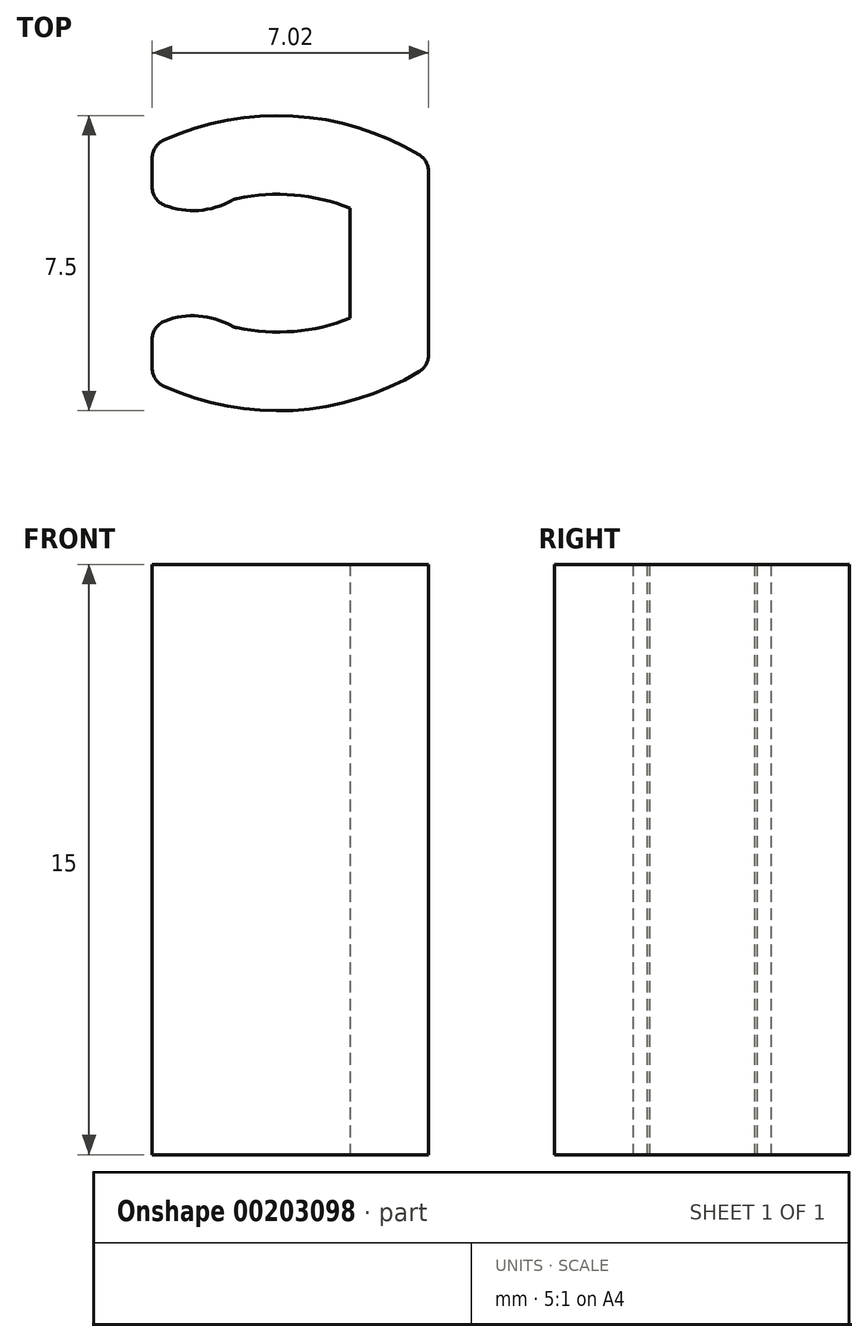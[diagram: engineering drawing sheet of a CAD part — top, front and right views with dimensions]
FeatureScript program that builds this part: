
annotation { "Feature Type Name" : "Feature", "Feature Type Description" : "" }
export const myFeature = defineFeature(function(context is Context, id is Id, definition is map)
    precondition{}
    {
        {
            var Q0;
            Q0=qCreatedBy(makeId("Top.planeOp"),FACE);
            var sketch = newSketch(context, id + "F0", { "sketchPlane" : qUnion([Q0])});
            skLineSegment(sketch, "E0", {"start": v(0, -23.14) * mm, "end": v(0, -17.14) * mm});
            skLineSegment(sketch, "E1", {"start": v(0, -17.14) * mm, "end": v(-4.2, -17.14) * mm});
            skLineSegment(sketch, "E2", {"start": v(-4.2, -17.14) * mm, "end": v(-3.62, -18.14) * mm});
            skLineSegment(sketch, "E3", {"start": v(0, -23.14) * mm, "end": v(-4.2, -23.14) * mm});
            skLineSegment(sketch, "E4", {"start": v(-4.2, -23.14) * mm, "end": v(-3.63, -22.15) * mm});
            skLineSegment(sketch, "E5.0", {"start": v(2, -15.14) * mm, "end": v(-4.2, -15.14) * mm});
            skLineSegment(sketch, "E5.1", {"start": v(2, -25.14) * mm, "end": v(2, -15.14) * mm});
            skLineSegment(sketch, "E5.2", {"start": v(2, -25.14) * mm, "end": v(-4.2, -25.14) * mm});
            skLineSegment(sketch, "E6", {"start": v(-3.63, -22.15) * mm, "end": v(-5.63, -22.15) * mm});
            skLineSegment(sketch, "E7", {"start": v(-5.63, -22.15) * mm, "end": v(-5.63, -24.15) * mm});
            skLineSegment(sketch, "E8", {"start": v(-5.63, -24.15) * mm, "end": v(-4.2, -25.14) * mm});
            skLineSegment(sketch, "E9", {"start": v(-3.62, -18.14) * mm, "end": v(-5.62, -18.14) * mm});
            skLineSegment(sketch, "E10", {"start": v(-5.62, -18.14) * mm, "end": v(-5.62, -16.14) * mm});
            skLineSegment(sketch, "E11", {"start": v(-5.63, -16.14) * mm, "end": v(-4.2, -15.14) * mm});
            skArc(sketch, "E12", {"start": v(3.26, 1.4) * mm, "mid": v(1.8, 1.74) * mm, "end": v(0.31, 1.63) * mm});
            skArc(sketch, "E13.MirrorCS", {"start": v(3.26, -1.4) * mm, "mid": v(1.8, -1.74) * mm, "end": v(0.31, -1.63) * mm});
            skLineSegment(sketch, "E14", {"start": v(3.26, 1.4) * mm, "end": v(3.26, -1.4) * mm});
            skArc(sketch, "E15.0", {"start": v(5.26, 2.6) * mm, "mid": v(1.8, 3.74) * mm, "end": v(-1.76, 2.98) * mm});
            skLineSegment(sketch, "E15.1", {"start": v(5.26, 2.6) * mm, "end": v(5.26, -2.6) * mm});
            skArc(sketch, "E15.2", {"start": v(5.26, -2.6) * mm, "mid": v(1.8, -3.74) * mm, "end": v(-1.76, -2.98) * mm});
            skArc(sketch, "E16", {"start": v(-1.76, 1.62) * mm, "mid": v(-0.72, 1.34) * mm, "end": v(0.31, 1.62) * mm});
            skArc(sketch, "E17", {"start": v(0.31, -1.63) * mm, "mid": v(-0.72, -1.34) * mm, "end": v(-1.76, -1.63) * mm});
            skArc(sketch, "E18", {"start": v(13.99, -0.44) * mm, "mid": v(11.63, 0.28) * mm, "end": v(9.21, -0.22) * mm});
            skArc(sketch, "E19.MirrorCS", {"start": v(13.99, -3.24) * mm, "mid": v(11.63, -3.96) * mm, "end": v(9.21, -3.47) * mm});
            skLineSegment(sketch, "E20", {"start": v(13.99, -0.44) * mm, "end": v(13.99, -3.24) * mm});
            skLineSegment(sketch, "E21", {"start": v(9.21, -0.22) * mm, "end": v(9.21, -0.47) * mm});
            skLineSegment(sketch, "E22", {"start": v(9.21, -3.47) * mm, "end": v(9.21, -3.22) * mm});
            skArc(sketch, "E23.0", {"start": v(15.99, 0.56) * mm, "mid": v(12.25, 2.23) * mm, "end": v(8.21, 1.52) * mm});
            skLineSegment(sketch, "E23.1", {"start": v(15.99, 0.56) * mm, "end": v(15.99, -4.25) * mm});
            skArc(sketch, "E23.2", {"start": v(15.99, -4.25) * mm, "mid": v(12.25, -5.92) * mm, "end": v(8.21, -5.2) * mm});
            skLineSegment(sketch, "E24", {"start": v(8.21, 1.52) * mm, "end": v(8.21, -0.47) * mm});
            skArc(sketch, "E25", {"start": v(8.21, -0.47) * mm, "mid": v(8.71, -0.53) * mm, "end": v(9.21, -0.47) * mm});
            skArc(sketch, "E26", {"start": v(9.21, -3.22) * mm, "mid": v(8.71, -3.15) * mm, "end": v(8.21, -3.22) * mm});
            skLineSegment(sketch, "E27.trimOffspring", {"start": v(8.21, -3.22) * mm, "end": v(8.21, -5.2) * mm});
            skLineSegment(sketch, "E28", {"start": v(-1.76, -2.98) * mm, "end": v(-1.76, -1.63) * mm});
            skLineSegment(sketch, "E29", {"start": v(-1.76, 1.62) * mm, "end": v(-1.76, 2.98) * mm});
            skSolve(sketch);
        }
        {
            var Q0;
            Q0=makeQuery(id+"F0.imprint","IMPRINT",FACE,{"disambiguationData":[TD([[makeQuery(id+"F0.imprint","IMPRINT",EDGE,{"derivedFrom":sQuery(id+"F0.wireOp",EDGE,"E12")}),-1.0]])]});
            extrude(context, id + "F1", {"entities" : qUnion([Q0]), "depth" : 15 * mm});
        }
        {
            var Q0;
            Q0=makeQuery(id+"F1.opExtrude","SWEPT_EDGE",EDGE,{"disambiguationData":[OSD([sQuery(id+"F0.wireOp",EDGE,"UlcmvIPN-8NSH-pf2d-Poad-CXsWTF12sEFO"),sQuery(id+"F0.wireOp",EDGE,"E16")])]});
            var Q1;
            Q1=makeQuery(id+"F1.opExtrude","SWEPT_EDGE",EDGE,{"disambiguationData":[OSD([sQuery(id+"F0.wireOp",EDGE,"FM8bWOw8-aIkb-mtE4-fcvr-1huLvntU2rRJ"),sQuery(id+"F0.wireOp",EDGE,"E16")])]});
            var Q2;
            Q2=makeQuery(id+"F1.opExtrude","SWEPT_EDGE",EDGE,{"disambiguationData":[OSD([sQuery(id+"F0.wireOp",EDGE,"sPA6GIjj-Ui0D-myYm-Dkea-vZuirA1r2ZR1"),sQuery(id+"F0.wireOp",EDGE,"E17")])]});
            var Q3;
            Q3=makeQuery(id+"F1.opExtrude","SWEPT_EDGE",EDGE,{"disambiguationData":[OSD([sQuery(id+"F0.wireOp",EDGE,"E17"),sQuery(id+"F0.wireOp",EDGE,"f8e81a8a-3d9e-42a9-b35c-d29aa75cf38c.trimOffspring")])]});
            var Q4;
            Q4=makeQuery(id+"F1.opExtrude","SWEPT_EDGE",EDGE,{"disambiguationData":[OSD([sQuery(id+"F0.wireOp",EDGE,"E15.0"),sQuery(id+"F0.wireOp",EDGE,"UlcmvIPN-8NSH-pf2d-Poad-CXsWTF12sEFO")])]});
            var Q5;
            Q5=makeQuery(id+"F1.opExtrude","SWEPT_EDGE",EDGE,{"disambiguationData":[OSD([sQuery(id+"F0.wireOp",EDGE,"E15.2"),sQuery(id+"F0.wireOp",EDGE,"f8e81a8a-3d9e-42a9-b35c-d29aa75cf38c.trimOffspring")])]});
            fillet(context, id + "F2", {"entities" : qUnion([Q0, Q1, Q2, Q3, Q4, Q5]), "radius" : .5 * mm, "tangentPropagation" : true, "allowEdgeOverflow" : false});
        }
    });
